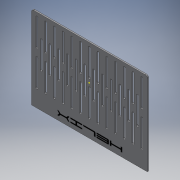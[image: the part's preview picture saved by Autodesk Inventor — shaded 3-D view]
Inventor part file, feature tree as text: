
AUTODESK INVENTOR PART (.ipt)
format: ipt  version: 2019 (Build 230136000, 136)  size: 418,816 bytes
history: native  units: mm
features: reference x6, extrude x5, sketch x5, other x5, fillet x2, helix x1
ambient origin geometry x8: Origin, YZ Plane, XZ Plane, XY Plane, X Axis, Y Axis, Z Axis, Center Point
bodies: Solid1 (feature_tree)
feature tree (24):
  extrude  "Extrusion1"  Depth=160.0mm
  extrude  "Extrusion2"  Depth=5.0mm
  fillet  "Fillet1"  Radius=5.0mm
  extrude  "Extrusion3"  Depth=10.0mm
  sketch  "Sketch4"  dims[d9=20.0mm d10=60.0mm]
  fillet  "Fillet2"  Radius=10.0mm
  extrude  "Extrusion4"  Depth=60.0mm
  extrude  "Extrusion5"  Depth=5.0mm
  sketch  "Sketch1"  dims[d0=265.0mm d1=160.0mm]
  sketch  "Sketch2"  dims[d2=3.0mm d3=0.0mm d4=5.0mm d5=5.0mm]
  sketch  "Sketch3"  dims[d6=10.0mm d7=10.0mm d8=10.0mm]
  sketch  "Sketch5"  dims[d11=5.0mm d12=5.0mm d13=60.0mm d14=50.0mm d15=130.0mm d17=20.0mm d18=10.0mm d20=10.0mm d22=3.0mm d23=0.0mm d24=5.0mm d25=30.0mm d26=3.0mm d27=0.0mm d28=5.0mm d29=3.0mm d30=0.0mm d31=3.0mm d32=0.0mm]
  reference  "Reference1"
  reference  "Reference2"
  reference  "Reference3"
  reference  "Reference4"
  reference  "Reference5"
  reference  "Reference6"
  other  "<userpath>\Documents\GitHub\Helix-DLP-3D-Printer\Helix DLP V2\Helix DLP V2.iam"
  helix  "Helix DLP V2.iam"  [1 undecoded]
  other  "Z Shaft:1"
  other  "Z Shaft:2"
  other  "support_shf16:2"
  other  "support_shf16:1"
note: 1 required parameter value undecoded (feature->parameter linkage not recoverable at this tier; creation-order binding heuristic only, values carry confidence <= 0.55)
